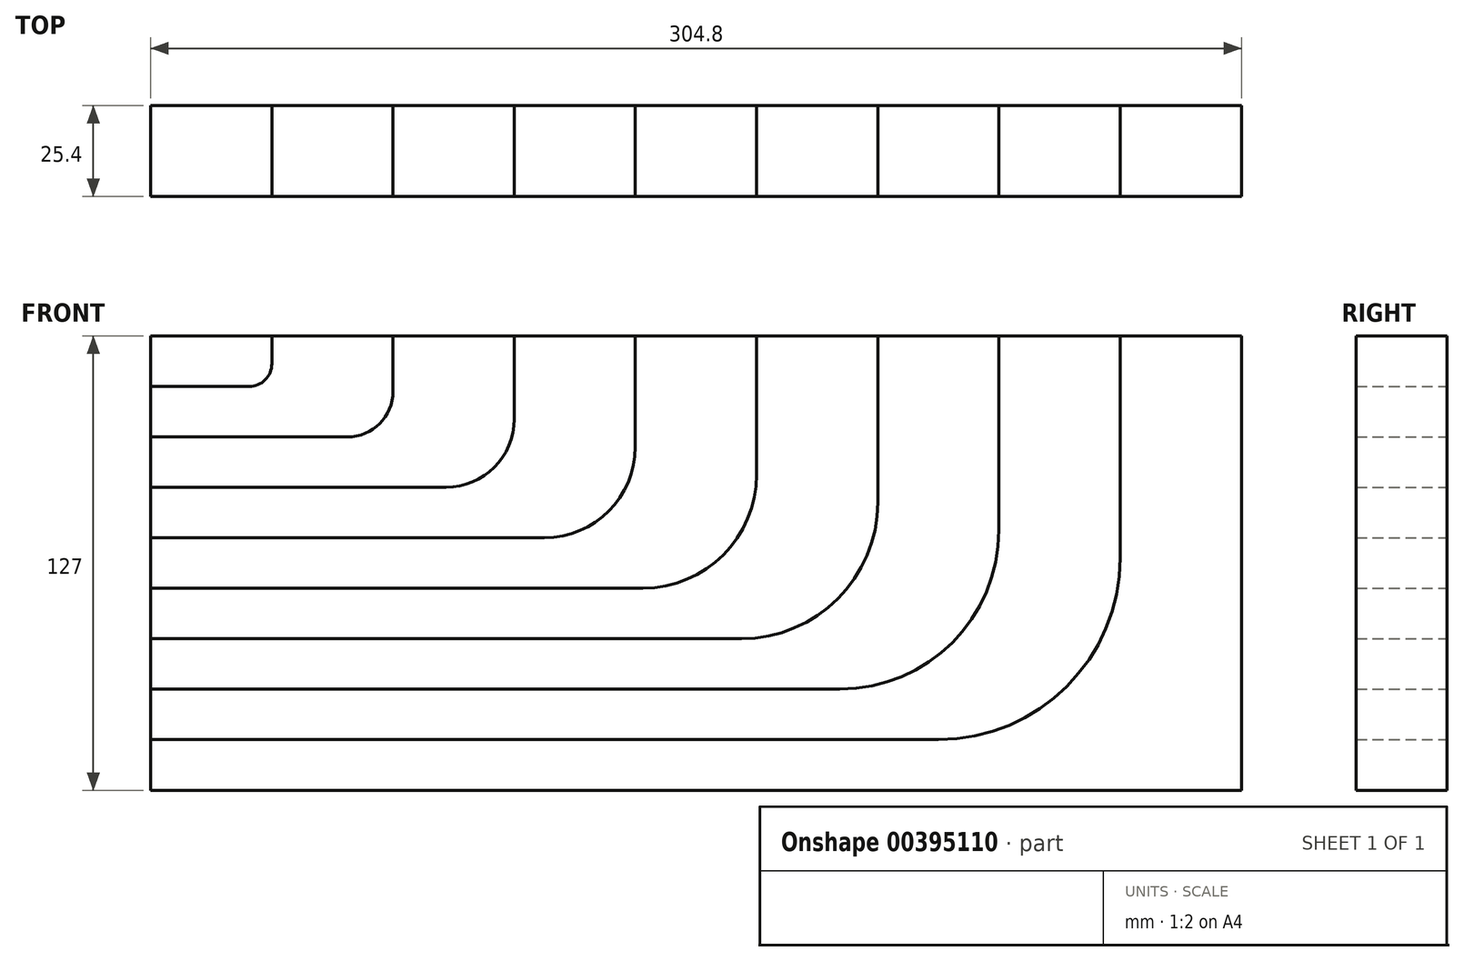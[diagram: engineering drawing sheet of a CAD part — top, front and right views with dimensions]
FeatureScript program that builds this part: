
annotation { "Feature Type Name" : "Feature", "Feature Type Description" : "" }
export const myFeature = defineFeature(function(context is Context, id is Id, definition is map)
    precondition{}
    {
        {
            var Q0;
            Q0=qCreatedBy(makeId("Front.planeOp"),FACE);
            var sketch = newSketch(context, id + "F0", { "sketchPlane" : qUnion([Q0])});
            skLineSegment(sketch, "E0.bottom", {"start": v(177.8, 63.5) * mm, "end": v(-127, 63.5) * mm});
            skLineSegment(sketch, "E0.top", {"start": v(177.8, -63.5) * mm, "end": v(-127, -63.5) * mm});
            skLineSegment(sketch, "E0.left", {"start": v(177.8, 63.5) * mm, "end": v(177.8, -63.5) * mm});
            skLineSegment(sketch, "E0.right", {"start": v(-127, 63.5) * mm, "end": v(-127, -63.5) * mm});
            skLineSegment(sketch, "E1.1.0.0", {"start": v(-93.14, 63.5) * mm, "end": v(-93.14, 55.75) * mm});
            skLineSegment(sketch, "E1.2.0.0", {"start": v(-59.28, 63.5) * mm, "end": v(-59.28, 48) * mm});
            skLineSegment(sketch, "E1.3.0.0", {"start": v(-25.43, 63.5) * mm, "end": v(-25.43, 40.26) * mm});
            skLineSegment(sketch, "E1.4.0.0", {"start": v(8.43, 63.5) * mm, "end": v(8.43, 32.51) * mm});
            skLineSegment(sketch, "E1.5.0.0", {"start": v(42.3, 63.5) * mm, "end": v(42.3, 24.77) * mm});
            skLineSegment(sketch, "E1.6.0.0", {"start": v(76.15, 63.5) * mm, "end": v(76.15, 17.02) * mm});
            skLineSegment(sketch, "E1.7.0.0", {"start": v(110, 63.5) * mm, "end": v(110, 9.27) * mm});
            skLineSegment(sketch, "E1.8.0.0", {"start": v(143.87, 63.5) * mm, "end": v(143.87, 1.52) * mm});
            skLineSegment(sketch, "E1.direction1", {"start": v(-127, -63.5) * mm, "end": v(-93.14, -63.5) * mm, "construction": true});
            skLineSegment(sketch, "E2.0.1.0", {"start": v(-99.5, 49.4) * mm, "end": v(-127, 49.4) * mm});
            skLineSegment(sketch, "E2.0.2.0", {"start": v(-71.98, 35.3) * mm, "end": v(-127, 35.3) * mm});
            skLineSegment(sketch, "E2.0.3.0", {"start": v(-44.48, 21.2) * mm, "end": v(-127, 21.2) * mm});
            skLineSegment(sketch, "E2.0.4.0", {"start": v(-16.97, 7.11) * mm, "end": v(-127, 7.11) * mm});
            skLineSegment(sketch, "E2.0.5.0", {"start": v(10.54, -6.98) * mm, "end": v(-127, -6.98) * mm});
            skLineSegment(sketch, "E2.0.6.0", {"start": v(38.05, -21.08) * mm, "end": v(-127, -21.08) * mm});
            skLineSegment(sketch, "E2.0.7.0", {"start": v(65.56, -35.18) * mm, "end": v(-127, -35.18) * mm});
            skLineSegment(sketch, "E2.0.8.0", {"start": v(93.07, -49.28) * mm, "end": v(-127, -49.28) * mm});
            skLineSegment(sketch, "E2.direction1", {"start": v(-127, 63.5) * mm, "end": v(-101.6, 63.5) * mm, "construction": true});
            skLineSegment(sketch, "E2.direction2", {"start": v(-127, 63.5) * mm, "end": v(-127, 49.4) * mm, "construction": true});
            skPoint(sketch, "E3.newPointA", {"position": v(-93.14, -63.5) * mm});
            skPoint(sketch, "E3.newPointB", {"position": v(177.8, 49.4) * mm});
            skArc(sketch, "E3.filletArc", {"start": v(-99.5, 49.4) * mm, "mid": v(-95, 51.26) * mm, "end": v(-93.14, 55.75) * mm});
            skPoint(sketch, "E4.newPointA", {"position": v(-59.28, -63.5) * mm});
            skPoint(sketch, "E4.newPointB", {"position": v(177.8, 35.3) * mm});
            skArc(sketch, "E4.filletArc", {"start": v(-71.98, 35.3) * mm, "mid": v(-63, 39.03) * mm, "end": v(-59.28, 48) * mm});
            skPoint(sketch, "E5.newPointA", {"position": v(-25.43, -63.5) * mm});
            skPoint(sketch, "E5.newPointB", {"position": v(177.8, 21.2) * mm});
            skArc(sketch, "E5.filletArc", {"start": v(-44.48, 21.2) * mm, "mid": v(-31, 26.79) * mm, "end": v(-25.43, 40.26) * mm});
            skPoint(sketch, "E6.newPointA", {"position": v(8.43, -63.5) * mm});
            skPoint(sketch, "E6.newPointB", {"position": v(177.8, 7.11) * mm});
            skArc(sketch, "E6.filletArc", {"start": v(-16.97, 7.11) * mm, "mid": v(1, 14.55) * mm, "end": v(8.43, 32.51) * mm});
            skPoint(sketch, "E7.newPointA", {"position": v(42.3, -63.5) * mm});
            skPoint(sketch, "E7.newPointB", {"position": v(177.8, -6.98) * mm});
            skArc(sketch, "E7.filletArc", {"start": v(10.54, -6.98) * mm, "mid": v(33, 2.31) * mm, "end": v(42.3, 24.77) * mm});
            skPoint(sketch, "E8.newPointA", {"position": v(76.15, -63.5) * mm});
            skPoint(sketch, "E8.newPointB", {"position": v(177.8, -21.08) * mm});
            skArc(sketch, "E8.filletArc", {"start": v(38.05, -21.08) * mm, "mid": v(64.99, -9.92) * mm, "end": v(76.15, 17.02) * mm});
            skPoint(sketch, "E9.newPointA", {"position": v(110, -63.5) * mm});
            skPoint(sketch, "E9.newPointB", {"position": v(177.8, -35.18) * mm});
            skArc(sketch, "E9.filletArc", {"start": v(65.56, -35.18) * mm, "mid": v(96.99, -22.16) * mm, "end": v(110, 9.27) * mm});
            skPoint(sketch, "E10.newPointA", {"position": v(143.87, -63.5) * mm});
            skPoint(sketch, "E10.newPointB", {"position": v(177.8, -49.28) * mm});
            skArc(sketch, "E10.filletArc", {"start": v(93.07, -49.28) * mm, "mid": v(128.99, -34.4) * mm, "end": v(143.87, 1.52) * mm});
            skSolve(sketch);
        }
        {
            var Q0;
            {var subQ0=sQuery(id+"F0.wireOp",EDGE,"E1.1.0.0");Q0=makeQuery(id+"F0.imprint","IMPRINT",FACE,{"disambiguationData":[TD([[makeQuery(id+"F0.imprint","IMPRINT",EDGE,{"derivedFrom":subQ0}),-1.0]])]});}
            var Q1;
            {var subQ4=sQuery(id+"F0.wireOp",EDGE,"E1.2.0.0");Q1=makeQuery(id+"F0.imprint","IMPRINT",FACE,{"disambiguationData":[TD([[makeQuery(id+"F0.imprint","IMPRINT",EDGE,{"derivedFrom":subQ4}),1.0]])]});}
            var Q2;
            {var subQ0=sQuery(id+"F0.wireOp",EDGE,"E1.4.0.0");Q2=makeQuery(id+"F0.imprint","IMPRINT",FACE,{"disambiguationData":[TD([[makeQuery(id+"F0.imprint","IMPRINT",EDGE,{"derivedFrom":subQ0}),1.0]])]});}
            var Q3;
            {var subQ1=sQuery(id+"F0.wireOp",EDGE,"E1.6.0.0");Q3=makeQuery(id+"F0.imprint","IMPRINT",FACE,{"disambiguationData":[TD([[makeQuery(id+"F0.imprint","IMPRINT",EDGE,{"derivedFrom":subQ1}),1.0]])]});}
            var Q4;
            {var subQ1=sQuery(id+"F0.wireOp",EDGE,"E0.top");Q4=makeQuery(id+"F0.imprint","IMPRINT",FACE,{"disambiguationData":[TD([[makeQuery(id+"F0.imprint","IMPRINT",EDGE,{"derivedFrom":subQ1}),-1.0]])]});}
            extrude(context, id + "F1", {"entities" : qUnion([Q0, Q1, Q2, Q3, Q4]), "depth" : 25.4 * mm});
        }
        {
            var Q0;
            {var subQ4=sQuery(id+"F0.wireOp",EDGE,"E1.7.0.0");Q0=makeQuery(id+"F0.imprint","IMPRINT",FACE,{"disambiguationData":[TD([[makeQuery(id+"F0.imprint","IMPRINT",EDGE,{"derivedFrom":subQ4}),1.0]])]});}
            var Q1;
            {var subQ1=sQuery(id+"F0.wireOp",EDGE,"E1.5.0.0");Q1=makeQuery(id+"F0.imprint","IMPRINT",FACE,{"disambiguationData":[TD([[makeQuery(id+"F0.imprint","IMPRINT",EDGE,{"derivedFrom":subQ1}),1.0]])]});}
            var Q2;
            {var subQ1=sQuery(id+"F0.wireOp",EDGE,"E1.3.0.0");Q2=makeQuery(id+"F0.imprint","IMPRINT",FACE,{"disambiguationData":[TD([[makeQuery(id+"F0.imprint","IMPRINT",EDGE,{"derivedFrom":subQ1}),1.0]])]});}
            var Q3;
            {var subQ1=sQuery(id+"F0.wireOp",EDGE,"E1.1.0.0");Q3=makeQuery(id+"F0.imprint","IMPRINT",FACE,{"disambiguationData":[TD([[makeQuery(id+"F0.imprint","IMPRINT",EDGE,{"derivedFrom":subQ1}),1.0]])]});}
            extrude(context, id + "F2", {"entities" : qUnion([Q0, Q1, Q2, Q3]), "depth" : 25.4 * mm});
        }
    });
